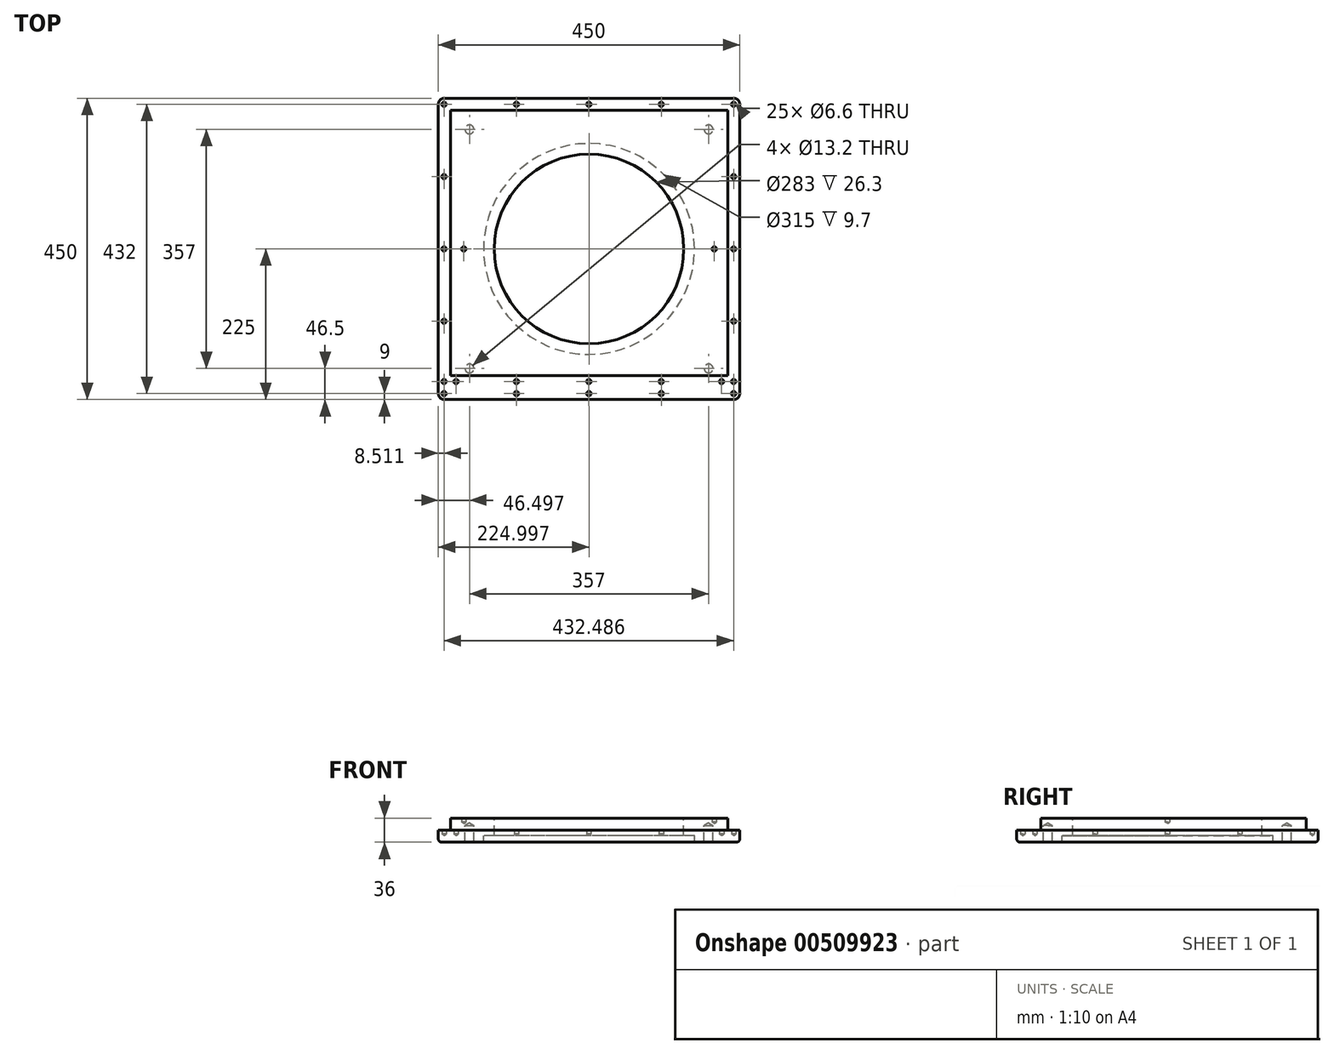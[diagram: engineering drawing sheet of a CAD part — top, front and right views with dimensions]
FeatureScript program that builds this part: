
annotation { "Feature Type Name" : "Feature", "Feature Type Description" : "" }
export const myFeature = defineFeature(function(context is Context, id is Id, definition is map)
    precondition{}
    {
        {
            var Q0;
            Q0=qCreatedBy(makeId("Front.planeOp"),FACE);
            var sketch = newSketch(context, id + "F0", { "sketchPlane" : qUnion([Q0])});
            skLineSegment(sketch, "E0.bottom", {"start": v(224.76, 7.53) * mm, "end": v(-225.24, 7.53) * mm});
            skLineSegment(sketch, "E0.top", {"start": v(224.76, -10.47) * mm, "end": v(-225.24, -10.47) * mm});
            skLineSegment(sketch, "E0.left", {"start": v(224.76, 7.53) * mm, "end": v(224.76, -10.47) * mm});
            skLineSegment(sketch, "E0.right", {"start": v(-225.24, 7.53) * mm, "end": v(-225.24, -10.47) * mm});
            skPoint(sketch, "E0.middle", {"position": v(0, 0) * mm});
            skSolve(sketch);
        }
        {
            var Q0;
            Q0=qSketchRegion(id+"F0",true);
            extrude(context, id + "F1", {"entities" : qUnion([Q0]), "depth" : 450 * mm});
        }
        {
            var Q0;
            Q0=makeQuery(id+"F1.opExtrude","SWEPT_FACE",FACE,{"disambiguationData":[OSD([sQuery(id+"F0.wireOp",EDGE,"E0.bottom")])]});
            var sketch = newSketch(context, id + "F2", { "sketchPlane" : qUnion([Q0])});
            skLineSegment(sketch, "E1", {"start": v(-225.24, -225) * mm, "end": v(224.76, -225) * mm});
            skLineSegment(sketch, "E2", {"start": v(-0.24, 0) * mm, "end": v(-0.24, -450) * mm});
            skPoint(sketch, "E3", {"position": v(-0.24, -225) * mm});
            skSolve(sketch);
        }
        {
            var Q0;
            Q0=sQuery(id+"F2.wireOp",VERTEX,"E3");
            var Q1;
            Q1=makeQuery(id+"F1.opExtrude","SWEPT_BODY",BODY,{"disambiguationData":[OSD([sQuery(id+"F0.wireOp",EDGE,"E0.bottom"),sQuery(id+"F0.wireOp",EDGE,"E0.top"),sQuery(id+"F0.wireOp",EDGE,"E0.left"),sQuery(id+"F0.wireOp",EDGE,"E0.right")])]});
            hole(context, id + "F3", {"style" : HoleStyle.C_BORE, "endStyle" : HoleEndStyle.BLIND, "holeDiameter" : 283 * mm, "cBoreDiameter" : 315 * mm, "cBoreDepth" : 9.7 * mm, "holeDepth" : 36 * mm, "isTappedThrough" : true, "tappedDepth" : 12 * mm, "tapClearance" : 3, "locations" : qUnion([Q0]), "scope" : qUnion([Q1])});
        }
        {
            var Q0;
            Q0=makeQuery(id+"F1.opExtrude","CAP_EDGE",EDGE,{"disambiguationData":[OSD([sQuery(id+"F0.wireOp",EDGE,"E0.right")])],"isStart":false});
            var Q1;
            Q1=makeQuery(id+"F1.opExtrude","CAP_EDGE",EDGE,{"disambiguationData":[OSD([sQuery(id+"F0.wireOp",EDGE,"E0.right")])],"isStart":true});
            var Q2;
            Q2=makeQuery(id+"F1.opExtrude","CAP_EDGE",EDGE,{"disambiguationData":[OSD([sQuery(id+"F0.wireOp",EDGE,"E0.left")])],"isStart":true});
            var Q3;
            Q3=makeQuery(id+"F1.opExtrude","CAP_EDGE",EDGE,{"disambiguationData":[OSD([sQuery(id+"F0.wireOp",EDGE,"E0.left")])],"isStart":false});
            fillet(context, id + "F4", {"entities" : qUnion([Q0, Q1, Q2, Q3]), "radius" : 9 * mm, "tangentPropagation" : true, "allowEdgeOverflow" : false});
        }
        {
            var Q0;
            Q0=makeQuery(id+"F1.opExtrude","CAP_EDGE",EDGE,{"disambiguationData":[OSD([sQuery(id+"F0.wireOp",EDGE,"E0.bottom")])],"isStart":true});
            var Q1;
            Q1=makeQuery(id+"F1.opExtrude","SWEPT_EDGE",EDGE,{"disambiguationData":[OSD([sQuery(id+"F0.wireOp",EDGE,"E0.bottom"),sQuery(id+"F0.wireOp",EDGE,"E0.left")])]});
            var Q2;
            Q2=makeQuery(id+"F1.opExtrude","CAP_EDGE",EDGE,{"disambiguationData":[OSD([sQuery(id+"F0.wireOp",EDGE,"E0.bottom")])],"isStart":false});
            var Q3;
            Q3=makeQuery(id+"F1.opExtrude","SWEPT_EDGE",EDGE,{"disambiguationData":[OSD([sQuery(id+"F0.wireOp",EDGE,"E0.bottom"),sQuery(id+"F0.wireOp",EDGE,"E0.right")])]});
            fillet(context, id + "F5", {"entities" : qUnion([Q0, Q1, Q2, Q3]), "radius" : 5 * mm, "tangentPropagation" : true, "allowEdgeOverflow" : false});
        }
        {
            var Q0;
            Q0=makeQuery(id+"F1.opExtrude","SWEPT_FACE",FACE,{"disambiguationData":[OSD([sQuery(id+"F0.wireOp",EDGE,"E0.top")])]});
            var sketch = newSketch(context, id + "F6", { "sketchPlane" : qUnion([Q0])});
            skLineSegment(sketch, "E4", {"start": v(0, 0) * mm, "end": v(0, 450) * mm});
            skPoint(sketch, "E5", {"position": v(-216.24, 225) * mm});
            skPoint(sketch, "E6", {"position": v(-216.24, 333) * mm});
            skPoint(sketch, "E7", {"position": v(-216.24, 117) * mm});
            skPoint(sketch, "E8.MirrorP", {"position": v(216.24, 333) * mm});
            skPoint(sketch, "E9.MirrorP", {"position": v(216.24, 117) * mm});
            skPoint(sketch, "E10.MirrorP", {"position": v(216.24, 225) * mm});
            skPoint(sketch, "E11", {"position": v(-216.24, 441) * mm});
            skPoint(sketch, "E12", {"position": v(-216.24, 9) * mm});
            skPoint(sketch, "E13.MirrorP", {"position": v(216.24, 441) * mm});
            skPoint(sketch, "E14.MirrorP", {"position": v(216.24, 9) * mm});
            skLineSegment(sketch, "E15", {"start": v(-216.24, 9) * mm, "end": v(-216.24, 441) * mm});
            skLineSegment(sketch, "E16", {"start": v(-216.24, 225) * mm, "end": v(-216.24, 441) * mm});
            skLineSegment(sketch, "E17", {"start": v(-216.24, 9) * mm, "end": v(-216.24, 225) * mm});
            skLineSegment(sketch, "E18", {"start": v(-216.24, 9) * mm, "end": v(216.24, 9) * mm});
            skLineSegment(sketch, "E19", {"start": v(216.24, 441) * mm, "end": v(-216.24, 441) * mm});
            skPoint(sketch, "E20", {"position": v(0, 441) * mm});
            skPoint(sketch, "E21", {"position": v(0, 9) * mm});
            skLineSegment(sketch, "E22", {"start": v(-216.24, 9) * mm, "end": v(0, 9) * mm});
            skLineSegment(sketch, "E23", {"start": v(0, 9) * mm, "end": v(216.24, 9) * mm});
            skLineSegment(sketch, "E24", {"start": v(216.24, 441) * mm, "end": v(0, 441) * mm});
            skLineSegment(sketch, "E25", {"start": v(0, 441) * mm, "end": v(-216.24, 441) * mm});
            skPoint(sketch, "E26", {"position": v(-108.12, 441) * mm});
            skPoint(sketch, "E27", {"position": v(108.12, 441) * mm});
            skPoint(sketch, "E28", {"position": v(108.12, 9) * mm});
            skPoint(sketch, "E29", {"position": v(-108.12, 9) * mm});
            skPoint(sketch, "E30", {"position": v(-108.12, 423) * mm});
            skPoint(sketch, "E31", {"position": v(108.12, 423) * mm});
            skPoint(sketch, "E32", {"position": v(-198.24, 423) * mm});
            skPoint(sketch, "E33", {"position": v(198.24, 423) * mm});
            skLineSegment(sketch, "E34", {"start": v(216.24, 9) * mm, "end": v(216.24, 441) * mm});
            skPoint(sketch, "E35", {"position": v(0, 423) * mm});
            skPoint(sketch, "E36", {"position": v(-216.24, 423) * mm});
            skPoint(sketch, "E37", {"position": v(216.24, 423) * mm});
            skSolve(sketch);
        }
        {
            var Q0;
            Q0=sQuery(id+"F6.wireOp",VERTEX,"E25.end");
            var Q1;
            Q1=sQuery(id+"F6.wireOp",VERTEX,"E26");
            var Q2;
            Q2=sQuery(id+"F6.wireOp",VERTEX,"E20");
            var Q3;
            Q3=sQuery(id+"F6.wireOp",VERTEX,"E27");
            var Q4;
            Q4=sQuery(id+"F6.wireOp",VERTEX,"E13.MirrorP");
            var Q5;
            Q5=sQuery(id+"F6.wireOp",VERTEX,"E31");
            var Q6;
            Q6=sQuery(id+"F6.wireOp",VERTEX,"E35");
            var Q7;
            Q7=sQuery(id+"F6.wireOp",VERTEX,"E30");
            var Q8;
            Q8=sQuery(id+"F6.wireOp",VERTEX,"E32");
            var Q9;
            Q9=sQuery(id+"F6.wireOp",VERTEX,"E33");
            var Q10;
            Q10=sQuery(id+"F6.wireOp",VERTEX,"E8.MirrorP");
            var Q11;
            Q11=sQuery(id+"F6.wireOp",VERTEX,"E10.MirrorP");
            var Q12;
            Q12=sQuery(id+"F6.wireOp",VERTEX,"E9.MirrorP");
            var Q13;
            Q13=sQuery(id+"F6.wireOp",VERTEX,"E34.start");
            var Q14;
            Q14=sQuery(id+"F6.wireOp",VERTEX,"E28");
            var Q15;
            Q15=sQuery(id+"F6.wireOp",VERTEX,"E23.start");
            var Q16;
            Q16=sQuery(id+"F6.wireOp",VERTEX,"E29");
            var Q17;
            Q17=sQuery(id+"F6.wireOp",VERTEX,"E22.start");
            var Q18;
            Q18=sQuery(id+"F6.wireOp",VERTEX,"E7");
            var Q19;
            Q19=sQuery(id+"F6.wireOp",VERTEX,"E5");
            var Q20;
            Q20=sQuery(id+"F6.wireOp",VERTEX,"E6");
            var Q21;
            Q21=sQuery(id+"F6.wireOp",VERTEX,"E36");
            var Q22;
            Q22=sQuery(id+"F6.wireOp",VERTEX,"E37");
            var Q23;
            Q23=makeQuery(id+"F1.opExtrude","SWEPT_BODY",BODY,{"disambiguationData":[OSD([sQuery(id+"F0.wireOp",EDGE,"E0.bottom"),sQuery(id+"F0.wireOp",EDGE,"E0.top"),sQuery(id+"F0.wireOp",EDGE,"E0.left"),sQuery(id+"F0.wireOp",EDGE,"E0.right")])]});
            hole(context, id + "F7", {"style" : HoleStyle.SIMPLE, "endStyle" : HoleEndStyle.BLIND, "standardTappedOrClearance" : lookupTablePath({ "standard" : "ISO", "fit" : "Normal", "size" : "M6", "type" : "Clearance" }), "standardBlindInLast" : lookupTablePath({ "fit" : "Standard", "standard" : "ISO", "size" : "M6", "type" : "Clearance" }), "holeDiameter" : 6.6 * mm, "holeDepth" : 6 * mm, "isTappedThrough" : true, "tappedDepth" : 12 * mm, "tapClearance" : 3, "locations" : qUnion([Q0, Q1, Q2, Q3, Q4, Q5, Q6, Q7, Q8, Q9, Q10, Q11, Q12, Q13, Q14, Q15, Q16, Q17, Q18, Q19, Q20, Q21, Q22]), "scope" : qUnion([Q23])});
        }
        {
            var Q0;
            Q0=makeQuery(id+"F1.opExtrude","SWEPT_BODY",BODY,{"disambiguationData":[OSD([sQuery(id+"F0.wireOp",EDGE,"E0.bottom"),sQuery(id+"F0.wireOp",EDGE,"E0.top"),sQuery(id+"F0.wireOp",EDGE,"E0.left"),sQuery(id+"F0.wireOp",EDGE,"E0.right")])]});
            var Q1;
            Q1=makeQuery(id+"F1.opExtrude","SWEPT_EDGE",EDGE,{"disambiguationData":[OSD([sQuery(id+"F0.wireOp",EDGE,"E0.top"),sQuery(id+"F0.wireOp",EDGE,"E0.left")])]});
            var Q2;
            Q2=makeQuery(id+"F1.opExtrude","SWEPT_EDGE",EDGE,{"disambiguationData":[OSD([sQuery(id+"F0.wireOp",EDGE,"E0.top"),sQuery(id+"F0.wireOp",EDGE,"E0.left")])]});
            transform(context, id + "F8", {"entities" : qUnion([Q0]), "transformType" : TransformType.ROTATION, "transformAxis" : qUnion([Q2]), "angle" : 180 * degree, "makeCopy" : false});
        }
        {
            var Q0;
            Q0=makeQuery(id+"F1.opExtrude","SWEPT_FACE",FACE,{"disambiguationData":[OSD([sQuery(id+"F0.wireOp",EDGE,"E0.top")])]});
            var sketch = newSketch(context, id + "F9", { "sketchPlane" : qUnion([Q0])});
            skLineSegment(sketch, "E38.bottom", {"start": v(242.76, -18) * mm, "end": v(656.76, -18) * mm});
            skLineSegment(sketch, "E38.top", {"start": v(242.76, -414) * mm, "end": v(656.76, -414) * mm});
            skLineSegment(sketch, "E38.left", {"start": v(242.76, -18) * mm, "end": v(242.76, -414) * mm});
            skLineSegment(sketch, "E38.right", {"start": v(656.76, -18) * mm, "end": v(656.76, -414) * mm});
            skSolve(sketch);
        }
        {
            var Q0;
            Q0=makeQuery(id+"F9.imprint","IMPRINT",FACE,{"disambiguationData":[TD([[makeQuery(id+"F9.imprint","IMPRINT",EDGE,{"derivedFrom":sQuery(id+"F9.wireOp",EDGE,"E38.bottom")}),-1.0]])]});
            extrude(context, id + "F10", {"entities" : qUnion([Q0]), "operationType" : NewBodyOperationType.ADD, "depth" : 18 * mm});
        }
        {
            var Q0;
            Q0=makeQuery(id+"F1.opExtrude","SWEPT_FACE",FACE,{"disambiguationData":[OSD([sQuery(id+"F0.wireOp",EDGE,"E0.bottom")])]});
            var sketch = newSketch(context, id + "F11", { "sketchPlane" : qUnion([Q0])});
            skLineSegment(sketch, "E39.bottom", {"start": v(233.76, 441) * mm, "end": v(308.76, 441) * mm});
            skLineSegment(sketch, "E39.top", {"start": v(233.76, 366) * mm, "end": v(308.76, 366) * mm});
            skLineSegment(sketch, "E39.left", {"start": v(233.76, 441) * mm, "end": v(233.76, 366) * mm});
            skLineSegment(sketch, "E39.right", {"start": v(308.76, 441) * mm, "end": v(308.76, 366) * mm});
            skLineSegment(sketch, "E40", {"start": v(271.26, 441) * mm, "end": v(271.26, 366) * mm});
            skLineSegment(sketch, "E41", {"start": v(233.76, 403.5) * mm, "end": v(308.76, 403.5) * mm});
            skPoint(sketch, "E42", {"position": v(271.26, 403.5) * mm});
            skLineSegment(sketch, "E43", {"start": v(449.76, 445) * mm, "end": v(449.76, 5) * mm});
            skPoint(sketch, "E44.MirrorP", {"position": v(628.26, 403.5) * mm});
            skLineSegment(sketch, "E45", {"start": v(229.76, 225) * mm, "end": v(669.76, 225) * mm});
            skPoint(sketch, "E46.MirrorP", {"position": v(271.26, 46.5) * mm});
            skPoint(sketch, "E47.MirrorP", {"position": v(628.26, 46.5) * mm});
            skSolve(sketch);
        }
        {
            var Q0;
            Q0=makeQuery(id+"F10.opExtrude","CAP_FACE",FACE,{"disambiguationData":[OSD([sQuery(id+"F0.wireOp",EDGE,"E0.top"),sQuery(id+"F3.hole-0.sketch.wireOp",EDGE,"core_line_2"),sQuery(id+"F9.wireOp",EDGE,"E38.bottom"),sQuery(id+"F9.wireOp",EDGE,"E38.top"),sQuery(id+"F9.wireOp",EDGE,"E38.left"),sQuery(id+"F9.wireOp",EDGE,"E38.right")])],"isStart":false});
            var sketch = newSketch(context, id + "F12", { "sketchPlane" : qUnion([Q0])});
            skLineSegment(sketch, "E48", {"start": v(242.76, -225) * mm, "end": v(656.76, -225) * mm});
            skPoint(sketch, "E49", {"position": v(262.76, -225) * mm});
            skPoint(sketch, "E50", {"position": v(636.76, -225) * mm});
            skSolve(sketch);
        }
        {
            var Q0;
            Q0=sQuery(id+"F11.wireOp",VERTEX,"E47.MirrorP");
            var Q1;
            Q1=sQuery(id+"F11.wireOp",VERTEX,"E46.MirrorP");
            var Q2;
            Q2=sQuery(id+"F11.wireOp",VERTEX,"E42");
            var Q3;
            Q3=sQuery(id+"F11.wireOp",VERTEX,"E44.MirrorP");
            var Q4;
            Q4=makeQuery(id+"F1.opExtrude","SWEPT_BODY",BODY,{"disambiguationData":[OSD([sQuery(id+"F0.wireOp",EDGE,"E0.bottom"),sQuery(id+"F0.wireOp",EDGE,"E0.top"),sQuery(id+"F0.wireOp",EDGE,"E0.left"),sQuery(id+"F0.wireOp",EDGE,"E0.right")])]});
            hole(context, id + "F13", {"style" : HoleStyle.SIMPLE, "endStyle" : HoleEndStyle.BLIND, "standardTappedOrClearance" : lookupTablePath({ "standard" : "ISO", "fit" : "Normal", "size" : "M12", "type" : "Clearance" }), "standardBlindInLast" : lookupTablePath({ "fit" : "Standard", "standard" : "ISO", "size" : "M12", "type" : "Clearance" }), "holeDiameter" : 13.2 * mm, "holeDepth" : 25 * mm, "isTappedThrough" : true, "tappedDepth" : 12 * mm, "tapClearance" : 3, "locations" : qUnion([Q0, Q1, Q2, Q3]), "scope" : qUnion([Q4])});
        }
        {
            var Q0;
            Q0=sQuery(id+"F12.wireOp",VERTEX,"E49");
            var Q1;
            Q1=sQuery(id+"F12.wireOp",VERTEX,"E50");
            var Q2;
            Q2=makeQuery(id+"F1.opExtrude","SWEPT_BODY",BODY,{"disambiguationData":[OSD([sQuery(id+"F0.wireOp",EDGE,"E0.bottom"),sQuery(id+"F0.wireOp",EDGE,"E0.top"),sQuery(id+"F0.wireOp",EDGE,"E0.left"),sQuery(id+"F0.wireOp",EDGE,"E0.right")])]});
            hole(context, id + "F14", {"style" : HoleStyle.SIMPLE, "endStyle" : HoleEndStyle.BLIND, "standardTappedOrClearance" : lookupTablePath({ "standard" : "ISO", "fit" : "Normal", "size" : "M6", "type" : "Clearance" }), "standardBlindInLast" : lookupTablePath({ "fit" : "Standard", "standard" : "ISO", "size" : "M6", "type" : "Clearance" }), "holeDiameter" : 6.6 * mm, "holeDepth" : 6 * mm, "isTappedThrough" : true, "tappedDepth" : 12 * mm, "tapClearance" : 3, "locations" : qUnion([Q0, Q1]), "scope" : qUnion([Q2])});
        }
    });
